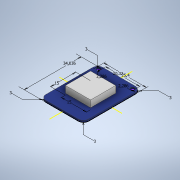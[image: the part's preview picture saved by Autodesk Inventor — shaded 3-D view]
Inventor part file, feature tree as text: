
AUTODESK INVENTOR PART (.ipt)
format: ipt  version: 2021 (Build 250183000, 183)  size: 136,704 bytes
history: native  units: mm
features: extrude x2, sketch x1
ambient origin geometry x8: Origin, YZ Plane, XZ Plane, XY Plane, X Axis, Y Axis, Z Axis, Center Point
bodies: Volumenkörper1 (feature_tree)
feature tree (3):
  sketch  "Skizze1"  dims[d0=25.4mm d1=34.036mm d2=2.286mm d3=2.286mm d4=20.32mm d5=3.0mm d6=3.0mm d7=3.0mm d8=3.0mm d9=15.0mm d10=15.0mm d12=1.0mm d13=0.0mm d14=5.0mm d15=0.0mm]
  extrude  "Extrusion1"  Depth=34.036mm
  extrude  "Extrusion2"  Depth=5.0mm
